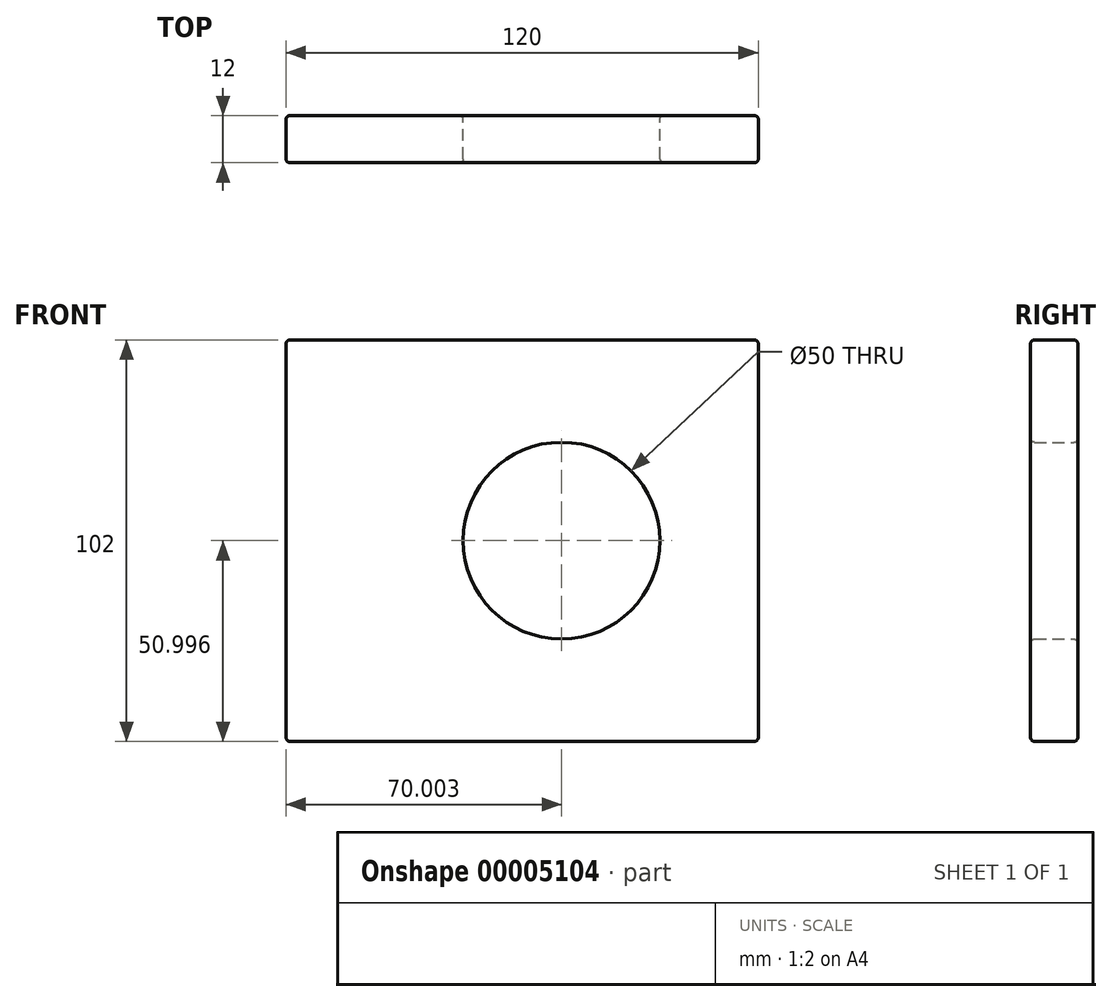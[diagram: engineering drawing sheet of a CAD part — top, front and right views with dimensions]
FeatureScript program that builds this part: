
annotation { "Feature Type Name" : "Feature", "Feature Type Description" : "" }
export const myFeature = defineFeature(function(context is Context, id is Id, definition is map)
    precondition{}
    {
        {
            var Q0;
            Q0=qCreatedBy(makeId("Front.planeOp"),FACE);
            var sketch = newSketch(context, id + "F0", { "sketchPlane" : qUnion([Q0])});
            skLineSegment(sketch, "E0.bottom", {"start": v(-68.85, 56.44) * mm, "end": v(51.15, 56.44) * mm});
            skLineSegment(sketch, "E0.top", {"start": v(-68.85, -45.56) * mm, "end": v(51.15, -45.56) * mm});
            skLineSegment(sketch, "E0.left", {"start": v(-68.85, 56.44) * mm, "end": v(-68.85, -45.56) * mm});
            skLineSegment(sketch, "E0.right", {"start": v(51.15, 56.44) * mm, "end": v(51.15, -45.56) * mm});
            skCircle(sketch, "E1", {"center": v(1.15, 5.44) * mm, "radius": 25 * mm});
            skSolve(sketch);
        }
        {
            var Q0;
            Q0=makeQuery(id+"F0.imprint","IMPRINT",FACE,{"disambiguationData":[TD([[makeQuery(id+"F0.imprint","IMPRINT",EDGE,{"derivedFrom":sQuery(id+"F0.wireOp",EDGE,"E0.bottom")}),-1.0]])]});
            extrude(context, id + "F1", {"entities" : qUnion([Q0]), "depth" : 12 * mm});
        }
        {
            var Q0;
            Q0=makeQuery(id+"F1.opExtrude","SWEPT_EDGE",EDGE,{"disambiguationData":[OSD([sQuery(id+"F0.wireOp",EDGE,"E0.bottom"),sQuery(id+"F0.wireOp",EDGE,"E0.left")])]});
            var Q1;
            Q1=makeQuery(id+"F1.opExtrude","CAP_EDGE",EDGE,{"disambiguationData":[OSD([sQuery(id+"F0.wireOp",EDGE,"E0.bottom")])],"isStart":false});
            var Q2;
            Q2=makeQuery(id+"F1.opExtrude","CAP_EDGE",EDGE,{"disambiguationData":[OSD([sQuery(id+"F0.wireOp",EDGE,"E0.bottom")])],"isStart":true});
            var Q3;
            Q3=makeQuery(id+"F1.opExtrude","SWEPT_EDGE",EDGE,{"disambiguationData":[OSD([sQuery(id+"F0.wireOp",EDGE,"E0.bottom"),sQuery(id+"F0.wireOp",EDGE,"E0.right")])]});
            var Q4;
            Q4=makeQuery(id+"F1.opExtrude","CAP_EDGE",EDGE,{"disambiguationData":[OSD([sQuery(id+"F0.wireOp",EDGE,"E0.right")])],"isStart":false});
            var Q5;
            Q5=makeQuery(id+"F1.opExtrude","CAP_EDGE",EDGE,{"disambiguationData":[OSD([sQuery(id+"F0.wireOp",EDGE,"E0.right")])],"isStart":true});
            var Q6;
            Q6=makeQuery(id+"F1.opExtrude","CAP_EDGE",EDGE,{"disambiguationData":[OSD([sQuery(id+"F0.wireOp",EDGE,"E1")])],"isStart":false});
            var Q7;
            Q7=makeQuery(id+"F1.opExtrude","SWEPT_EDGE",EDGE,{"disambiguationData":[OSD([sQuery(id+"F0.wireOp",EDGE,"E0.top"),sQuery(id+"F0.wireOp",EDGE,"E0.right")])]});
            var Q8;
            Q8=makeQuery(id+"F1.opExtrude","CAP_EDGE",EDGE,{"disambiguationData":[OSD([sQuery(id+"F0.wireOp",EDGE,"E0.top")])],"isStart":false});
            var Q9;
            Q9=makeQuery(id+"F1.opExtrude","CAP_EDGE",EDGE,{"disambiguationData":[OSD([sQuery(id+"F0.wireOp",EDGE,"E0.left")])],"isStart":false});
            var Q10;
            Q10=makeQuery(id+"F1.opExtrude","CAP_EDGE",EDGE,{"disambiguationData":[OSD([sQuery(id+"F0.wireOp",EDGE,"E0.left")])],"isStart":true});
            var Q11;
            Q11=makeQuery(id+"F1.opExtrude","SWEPT_FACE",FACE,{"disambiguationData":[OSD([sQuery(id+"F0.wireOp",EDGE,"E0.left")])]});
            var Q12;
            Q12=makeQuery(id+"F1.opExtrude","CAP_EDGE",EDGE,{"disambiguationData":[OSD([sQuery(id+"F0.wireOp",EDGE,"E0.top")])],"isStart":true});
            var Q13;
            Q13=makeQuery(id+"F1.opExtrude","CAP_EDGE",EDGE,{"disambiguationData":[OSD([sQuery(id+"F0.wireOp",EDGE,"E1")])],"isStart":true});
            fillet(context, id + "F2", {"entities" : qUnion([Q0, Q1, Q2, Q3, Q4, Q5, Q6, Q7, Q8, Q9, Q10, Q11, Q12, Q13]), "radius" : 1 * mm, "tangentPropagation" : true, "allowEdgeOverflow" : false});
        }
    });
